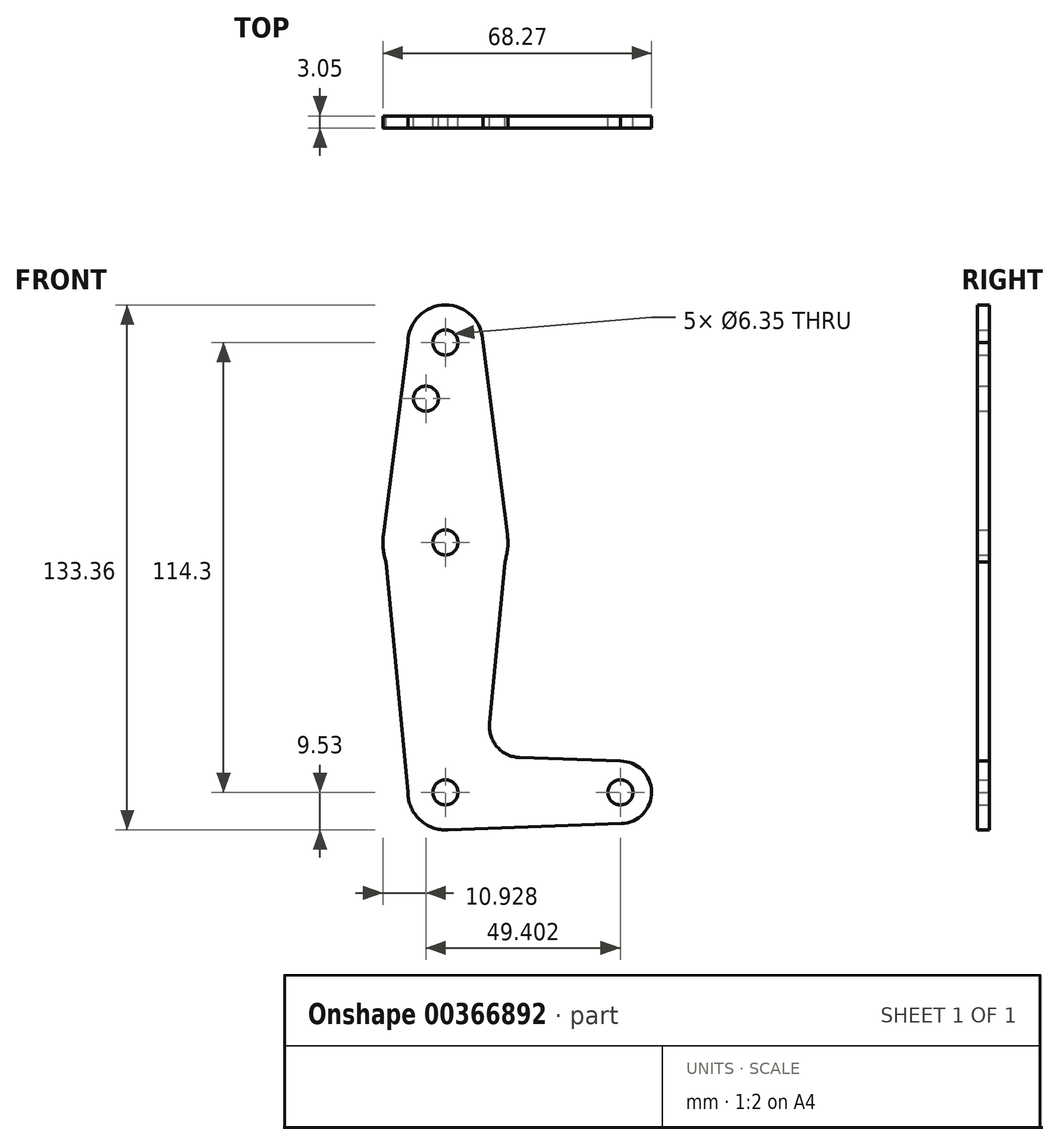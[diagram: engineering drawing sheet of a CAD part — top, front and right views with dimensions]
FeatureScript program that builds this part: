
annotation { "Feature Type Name" : "Feature", "Feature Type Description" : "" }
export const myFeature = defineFeature(function(context is Context, id is Id, definition is map)
    precondition{}
    {
        {
            var Q0;
            Q0=qCreatedBy(makeId("Front.planeOp"),FACE);
            var sketch = newSketch(context, id + "F0", { "sketchPlane" : qUnion([Q0])});
            skLineSegment(sketch, "E0", {"start": v(0, 114.3) * mm, "end": v(0, 0) * mm, "construction": true});
            skLineSegment(sketch, "E1", {"start": v(0, 0) * mm, "end": v(44.45, 0) * mm, "construction": true});
            skCircle(sketch, "E2", {"center": v(0, 114.3) * mm, "radius": 9.53 * mm});
            skCircle(sketch, "E3", {"center": v(0, 63.5) * mm, "radius": 15.88 * mm});
            skCircle(sketch, "E4", {"center": v(0, 0) * mm, "radius": 9.53 * mm});
            skCircle(sketch, "E5", {"center": v(44.45, 0) * mm, "radius": 7.94 * mm});
            skLineSegment(sketch, "E6", {"start": v(-9.53, 114.3) * mm, "end": v(-15.75, 65.5) * mm});
            skLineSegment(sketch, "E7", {"start": v(9.52, 114.3) * mm, "end": v(15.75, 65.5) * mm});
            skLineSegment(sketch, "E8", {"start": v(15.75, 65.5) * mm, "end": v(11.22, 17.54) * mm});
            skLineSegment(sketch, "E9", {"start": v(0, -9.52) * mm, "end": v(44.73, -7.93) * mm});
            skCircle(sketch, "E10", {"center": v(0, 114.3) * mm, "radius": 3.18 * mm});
            skCircle(sketch, "E11", {"center": v(-4.95, 100.03) * mm, "radius": 3.18 * mm});
            skCircle(sketch, "E12", {"center": v(0, 63.5) * mm, "radius": 3.18 * mm});
            skCircle(sketch, "E13", {"center": v(0, 0) * mm, "radius": 3.18 * mm});
            skCircle(sketch, "E14", {"center": v(44.45, 0) * mm, "radius": 3.18 * mm});
            skLineSegment(sketch, "E15", {"start": v(44.45, 7.94) * mm, "end": v(18.85, 8.85) * mm});
            skArc(sketch, "E16.filletArc", {"start": v(11.22, 17.54) * mm, "mid": v(13.16, 11.55) * mm, "end": v(18.85, 8.85) * mm});
            skLineSegment(sketch, "E17", {"start": v(-9.52, 0) * mm, "end": v(-15.75, 65.5) * mm});
            skSolve(sketch);
        }
        {
            var Q0;
            Q0 = qSketchRegion(id + "F0", true);
            extrude(context, id + "F1", {"entities" : qUnion([Q0]), "depth" : 3.05 * mm});
        }
    });
